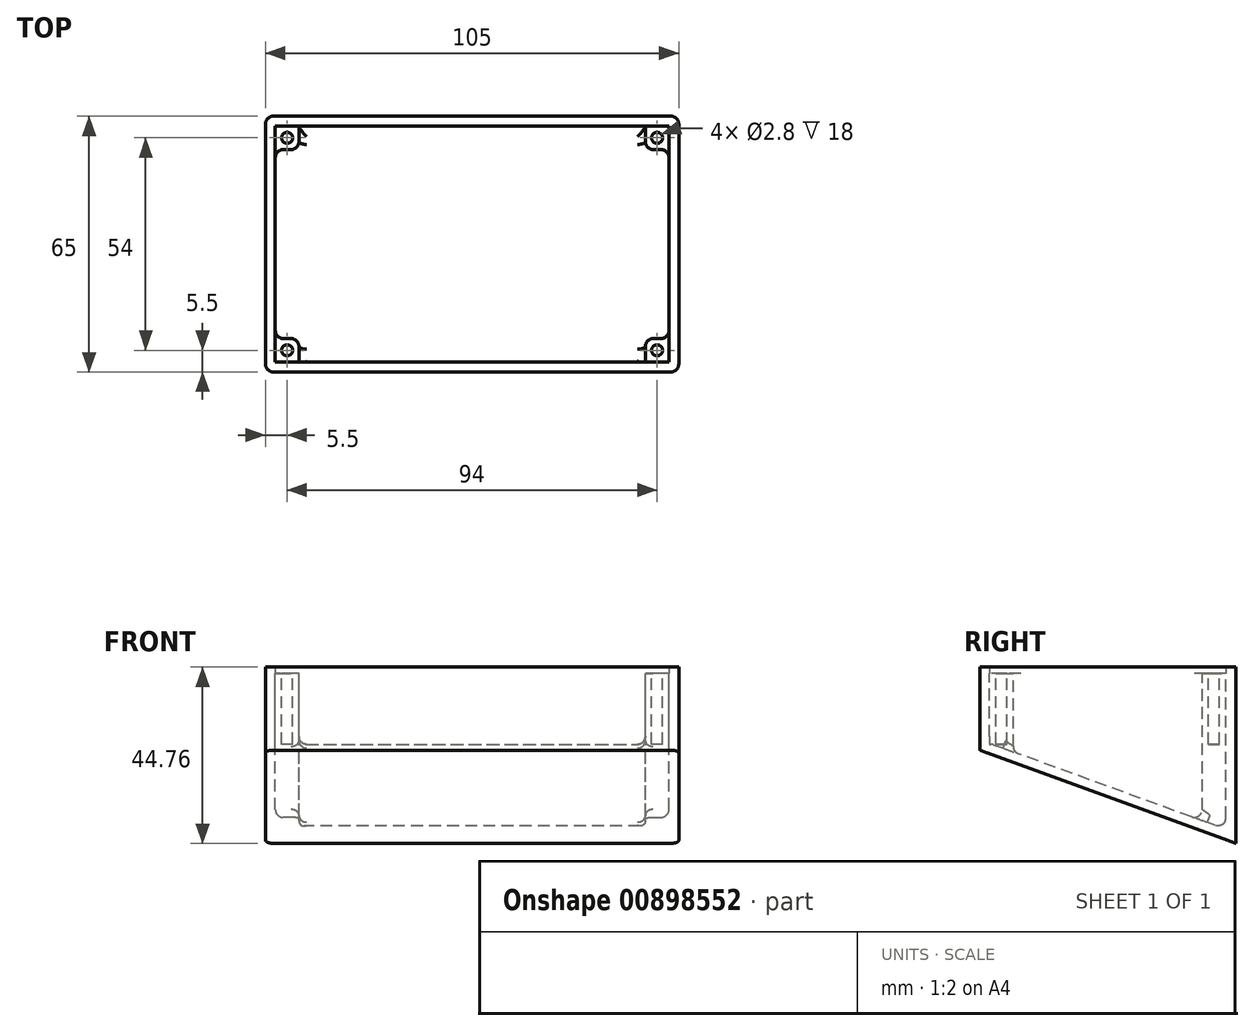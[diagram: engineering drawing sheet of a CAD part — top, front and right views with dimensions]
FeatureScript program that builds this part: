
annotation { "Feature Type Name" : "Feature", "Feature Type Description" : "" }
export const myFeature = defineFeature(function(context is Context, id is Id, definition is map)
    precondition{}
    {
        {
            var Q0;
            Q0=qCreatedBy(makeId("Top.planeOp"),FACE);
            var sketch = newSketch(context, id + "F0", { "sketchPlane" : qUnion([Q0])});
            skLineSegment(sketch, "E0", {"start": v(0, 30) * mm, "end": v(-50, 30) * mm});
            skLineSegment(sketch, "E1", {"start": v(-50, 30) * mm, "end": v(-50, 0) * mm});
            skLineSegment(sketch, "E2.MirrorCS", {"start": v(0, 30) * mm, "end": v(50, 30) * mm});
            skLineSegment(sketch, "E3.MirrorCS", {"start": v(50, 30) * mm, "end": v(50, 0) * mm});
            skLineSegment(sketch, "E4.MirrorCS", {"start": v(-50, -30) * mm, "end": v(-50, 0) * mm});
            skLineSegment(sketch, "E5.MirrorCS", {"start": v(0, -30) * mm, "end": v(-50, -30) * mm});
            skLineSegment(sketch, "E6.MirrorCS", {"start": v(0, -30) * mm, "end": v(50, -30) * mm});
            skLineSegment(sketch, "E7.MirrorCS", {"start": v(50, -30) * mm, "end": v(50, 0) * mm});
            skLineSegment(sketch, "E8", {"start": v(0, 32.5) * mm, "end": v(-52.5, 32.5) * mm});
            skLineSegment(sketch, "E9", {"start": v(-52.5, 32.5) * mm, "end": v(-52.5, 0) * mm});
            skLineSegment(sketch, "E10.MirrorCS", {"start": v(52.5, 32.5) * mm, "end": v(52.5, 0) * mm});
            skLineSegment(sketch, "E11.MirrorCS", {"start": v(0, 32.5) * mm, "end": v(52.5, 32.5) * mm});
            skLineSegment(sketch, "E12.MirrorCS", {"start": v(-52.5, -32.5) * mm, "end": v(-52.5, 0) * mm});
            skLineSegment(sketch, "E13.MirrorCS", {"start": v(0, -32.5) * mm, "end": v(-52.5, -32.5) * mm});
            skLineSegment(sketch, "E14.MirrorCS", {"start": v(0, -32.5) * mm, "end": v(52.5, -32.5) * mm});
            skLineSegment(sketch, "E15.MirrorCS", {"start": v(52.5, -32.5) * mm, "end": v(52.5, 0) * mm});
            skSolve(sketch);
        }
        {
            var Q0;
            Q0=makeQuery(id+"F0.imprint","IMPRINT",FACE,{"disambiguationData":[TD([[makeQuery(id+"F0.imprint","IMPRINT",EDGE,{"derivedFrom":sQuery(id+"F0.wireOp",EDGE,"E0")}),-1.0]])]});
            extrude(context, id + "F1", {"entities" : qUnion([Q0]), "depth" : 1.6 * mm, "offsetDistance" : 25 * mm});
        }
        {
            var Q0;
            Q0=qCreatedBy(makeId("Top.planeOp"),FACE);
            var sketch = newSketch(context, id + "F2", { "sketchPlane" : qUnion([Q0])});
            skLineSegment(sketch, "E16.0", {"start": v(-52.5, 32.5) * mm, "end": v(52.5, 32.5) * mm});
            skLineSegment(sketch, "E17.0", {"start": v(-52.5, 32.5) * mm, "end": v(-52.5, -32.5) * mm});
            skCircle(sketch, "E18", {"center": v(-47, 27) * mm, "radius": 1.4 * mm});
            skLineSegment(sketch, "E19", {"start": v(-50, 24) * mm, "end": v(-44, 24) * mm});
            skLineSegment(sketch, "E20", {"start": v(-44, 24) * mm, "end": v(-44, 30) * mm});
            skLineSegment(sketch, "E21.0", {"start": v(44, 30) * mm, "end": v(-44, 30) * mm});
            skLineSegment(sketch, "E22.0", {"start": v(-50, -30) * mm, "end": v(-50, 24) * mm});
            skPoint(sketch, "E23.orphan", {"position": v(-50, 30) * mm});
            skLineSegment(sketch, "E24.MirrorCS", {"start": v(-44, 30) * mm, "end": v(44, 30) * mm});
            skLineSegment(sketch, "E25.MirrorCS", {"start": v(52.5, 32.5) * mm, "end": v(-52.5, 32.5) * mm});
            skLineSegment(sketch, "E26.MirrorCS", {"start": v(44, 24) * mm, "end": v(44, 30) * mm});
            skLineSegment(sketch, "E27.MirrorCS", {"start": v(50, 24) * mm, "end": v(44, 24) * mm});
            skLineSegment(sketch, "E28.MirrorCS", {"start": v(52.5, 32.5) * mm, "end": v(52.5, -32.5) * mm});
            skLineSegment(sketch, "E29.MirrorCS", {"start": v(50, -30) * mm, "end": v(50, 24) * mm});
            skCircle(sketch, "E30.MirrorC", {"center": v(47, 27) * mm, "radius": 1.4 * mm});
            skPoint(sketch, "E31.orphan", {"position": v(50, 30) * mm});
            skLineSegment(sketch, "E32.MirrorCS", {"start": v(-50, 30) * mm, "end": v(-50, -24) * mm});
            skLineSegment(sketch, "E33.MirrorCS", {"start": v(-50, -24) * mm, "end": v(-44, -24) * mm});
            skLineSegment(sketch, "E34.MirrorCS", {"start": v(-44, -24) * mm, "end": v(-44, -30) * mm});
            skLineSegment(sketch, "E35.MirrorCS", {"start": v(-44, -30) * mm, "end": v(44, -30) * mm});
            skCircle(sketch, "E36.MirrorC", {"center": v(-47, -27) * mm, "radius": 1.4 * mm});
            skLineSegment(sketch, "E37.MirrorCS", {"start": v(52.5, -32.5) * mm, "end": v(-52.5, -32.5) * mm});
            skLineSegment(sketch, "E38.MirrorCS", {"start": v(-52.5, -32.5) * mm, "end": v(-52.5, 32.5) * mm});
            skLineSegment(sketch, "E39.MirrorCS", {"start": v(52.5, -32.5) * mm, "end": v(52.5, 32.5) * mm});
            skLineSegment(sketch, "E40.MirrorCS", {"start": v(50, -24) * mm, "end": v(44, -24) * mm});
            skLineSegment(sketch, "E41.MirrorCS", {"start": v(44, -24) * mm, "end": v(44, -30) * mm});
            skCircle(sketch, "E42.MirrorC", {"center": v(47, -27) * mm, "radius": 1.4 * mm});
            skSolve(sketch);
        }
        {
            var Q0;
            Q0 = qSketchRegion(id + "F2", true);
            extrude(context, id + "F3", {"entities" : qUnion([Q0]), "operationType" : NewBodyOperationType.ADD, "oppositeDirection" : true, "depth" : 18 * mm, "offsetDistance" : 25 * mm});
        }
        {
            var Q0;
            {var subQ0=sQuery(id+"F0.wireOp",EDGE,"E15.MirrorCS");var subQ1=sQuery(id+"F0.wireOp",EDGE,"E10.MirrorCS");Q0=makeQuery(id+"F3.boolean.opBoolean","MERGE",FACE,{"derivedFrom":[makeQuery(id+"F1.opExtrude","SWEPT_FACE",FACE,{"disambiguationData":[OSD([subQ1,subQ0])]}),makeQuery(id+"F3.opExtrude","SWEPT_FACE",FACE,{"disambiguationData":[OSD([subQ1,subQ0])]}),makeQuery(id+"F3.opExtrude","SWEPT_FACE",FACE,{"disambiguationData":[OSD([sQuery(id+"F2.wireOp",EDGE,"E39.MirrorCS")])]})]});}
            var sketch = newSketch(context, id + "F4", { "sketchPlane" : qUnion([Q0])});
            skLineSegment(sketch, "E43", {"start": v(-32.5, -18) * mm, "end": v(-32.5, -19.5) * mm});
            skLineSegment(sketch, "E44", {"start": v(-32.5, -19.5) * mm, "end": v(32.5, -43.16) * mm});
            skLineSegment(sketch, "E45", {"start": v(32.5, -43.16) * mm, "end": v(32.5, -18) * mm});
            skSolve(sketch);
        }
        {
            var Q0;
            Q0=makeQuery(id+"F4.imprint","IMPRINT",FACE,{"disambiguationData":[TD([[makeQuery(id+"F4.imprint","IMPRINT",EDGE,{"derivedFrom":sQuery(id+"F4.wireOp",EDGE,"E43")}),1.0]])]});
            extrude(context, id + "F5", {"entities" : qUnion([Q0]), "operationType" : NewBodyOperationType.ADD, "oppositeDirection" : true, "depth" : 1.5 * mm, "offsetDistance" : 25 * mm});
        }
        {
            var Q0;
            Q0=makeQuery(id+"F3.boolean.opBoolean","MERGE",FACE,{"derivedFrom":[makeQuery(id+"F1.opExtrude","SWEPT_FACE",FACE,{"disambiguationData":[OSD([sQuery(id+"F0.wireOp",EDGE,"E9"),sQuery(id+"F0.wireOp",EDGE,"E12.MirrorCS")])]}),makeQuery(id+"F3.opExtrude","SWEPT_FACE",FACE,{"disambiguationData":[OSD([sQuery(id+"F2.wireOp",EDGE,"E38.MirrorCS")])]})]});
            var sketch = newSketch(context, id + "F6", { "sketchPlane" : qUnion([Q0])});
            skLineSegment(sketch, "E46.0.3", {"start": v(-32.5, -43.16) * mm, "end": v(32.5, -19.5) * mm});
            skLineSegment(sketch, "E46.0.4", {"start": v(32.5, -19.5) * mm, "end": v(32.5, -18) * mm});
            skLineSegment(sketch, "E47.0", {"start": v(-32.5, -43.16) * mm, "end": v(-32.5, -18) * mm});
            skLineSegment(sketch, "E48", {"start": v(32.5, -18) * mm, "end": v(-32.5, -18) * mm});
            skLineSegment(sketch, "E49.0", {"start": v(32.5, -19.5) * mm, "end": v(-32.5, -43.16) * mm, "construction": true});
            skLineSegment(sketch, "E49.1", {"start": v(-32.5, 1.6) * mm, "end": v(-32.5, -43.16) * mm, "construction": true});
            skLineSegment(sketch, "E49.2", {"start": v(32.5, 1.6) * mm, "end": v(32.5, -19.5) * mm, "construction": true});
            skSolve(sketch);
        }
        {
            var Q0;
            Q0 = qSketchRegion(id + "F6", true);
            extrude(context, id + "F7", {"entities" : qUnion([Q0]), "operationType" : NewBodyOperationType.ADD, "oppositeDirection" : true, "depth" : 1.5 * mm, "offsetDistance" : 25 * mm});
        }
        {
            var Q0;
            Q0=makeQuery(id+"F5.opExtrude","CAP_FACE",FACE,{"disambiguationData":[OSD([sQuery(id+"F2.wireOp",EDGE,"E39.MirrorCS"),sQuery(id+"F4.wireOp",EDGE,"E43"),sQuery(id+"F4.wireOp",EDGE,"E44"),sQuery(id+"F4.wireOp",EDGE,"E45")])],"isStart":false});
            var sketch = newSketch(context, id + "F8", { "sketchPlane" : qUnion([Q0])});
            skLineSegment(sketch, "E50.0", {"start": v(-32.5, -43.16) * mm, "end": v(-32.5, -18) * mm});
            skLineSegment(sketch, "E51.0", {"start": v(32.5, -19.5) * mm, "end": v(-32.5, -43.16) * mm});
            skLineSegment(sketch, "E52.0", {"start": v(32.5, -18) * mm, "end": v(32.5, -19.5) * mm});
            skLineSegment(sketch, "E53", {"start": v(-30, -39.59) * mm, "end": v(29.31, -18) * mm});
            skLineSegment(sketch, "E54", {"start": v(-30, -18) * mm, "end": v(-30, -39.59) * mm});
            skLineSegment(sketch, "E55.0", {"start": v(-30, -18) * mm, "end": v(-32.5, -18) * mm});
            skLineSegment(sketch, "E56.0", {"start": v(32.5, -18) * mm, "end": v(-32.5, -18) * mm, "construction": true});
            skSolve(sketch);
        }
        {
            var Q0;
            Q0=makeQuery(id+"F8.imprint","IMPRINT",FACE,{"disambiguationData":[TD([[makeQuery(id+"F8.imprint","IMPRINT",EDGE,{"derivedFrom":sQuery(id+"F8.wireOp",EDGE,"E50.0")}),-1.0]])]});
            extrude(context, id + "F9", {"entities" : qUnion([Q0]), "operationType" : NewBodyOperationType.ADD, "endBound" : BoundingType.UP_TO_NEXT, "depth" : 25 * mm, "offsetDistance" : 25 * mm});
        }
        {
            var Q0;
            {var subQ0=sQuery(id+"F2.wireOp",EDGE,"E26.MirrorCS");var subQ1=makeQuery(id+"F3.opExtrude","SWEPT_FACE",FACE,{"disambiguationData":[OSD([subQ0])]});var subQ3=sQuery(id+"F2.wireOp",EDGE,"E39.MirrorCS");var subQ5=sQuery(id+"F2.wireOp",EDGE,"E24.MirrorCS");var subQ9=sQuery(id+"F2.wireOp",EDGE,"E27.MirrorCS");var subQ11=sQuery(id+"F2.wireOp",EDGE,"E29.MirrorCS");var subQ13=sQuery(id+"F2.wireOp",EDGE,"E30.MirrorC");var subQ15=sQuery(id+"F2.wireOp",EDGE,"E25.MirrorCS");var subQ16=sQuery(id+"F2.wireOp",EDGE,"E20");var subQ17=sQuery(id+"F2.wireOp",EDGE,"E18");var subQ18=sQuery(id+"F2.wireOp",EDGE,"E19");var subQ20=sQuery(id+"F2.wireOp",EDGE,"E32.MirrorCS");Q0=makeQuery(id+"F9.boolean.opBoolean","SPLIT",FACE,{"disambiguationData":[TD([subQ1])],"derivedFrom":makeQuery(id+"F7.boolean.opBoolean","SPLIT",FACE,{"disambiguationData":[TD([makeQuery(id+"F3.opExtrude","SWEPT_FACE",FACE,{"disambiguationData":[OSD([subQ17])]})])],"derivedFrom":makeQuery(id+"F3.opExtrude","CAP_FACE",FACE,{"disambiguationData":[OSD([subQ17,subQ18,subQ16,subQ5,subQ15,subQ0,subQ9,subQ11,subQ13,subQ20,sQuery(id+"F2.wireOp",EDGE,"E33.MirrorCS"),sQuery(id+"F2.wireOp",EDGE,"E34.MirrorCS"),sQuery(id+"F2.wireOp",EDGE,"E35.MirrorCS"),sQuery(id+"F2.wireOp",EDGE,"E36.MirrorC"),sQuery(id+"F2.wireOp",EDGE,"E37.MirrorCS"),sQuery(id+"F2.wireOp",EDGE,"E38.MirrorCS"),subQ3,sQuery(id+"F2.wireOp",EDGE,"E40.MirrorCS"),sQuery(id+"F2.wireOp",EDGE,"E41.MirrorCS"),sQuery(id+"F2.wireOp",EDGE,"E42.MirrorC")])],"isStart":false})})});}
            var sketch = newSketch(context, id + "F10", { "sketchPlane" : qUnion([Q0])});
            skLineSegment(sketch, "E57.0.0", {"start": v(-44, 30) * mm, "end": v(-50, 30) * mm});
            skLineSegment(sketch, "E57.0.1", {"start": v(-50, 30) * mm, "end": v(-50, 24) * mm});
            skLineSegment(sketch, "E57.0.2", {"start": v(-50, 24) * mm, "end": v(-44, 24) * mm});
            skLineSegment(sketch, "E57.0.3", {"start": v(-44, 24) * mm, "end": v(-44, 30) * mm});
            skLineSegment(sketch, "E58.0.0", {"start": v(-50, -24) * mm, "end": v(-50, -30) * mm});
            skLineSegment(sketch, "E58.0.1", {"start": v(-50, -30) * mm, "end": v(-44, -30) * mm});
            skLineSegment(sketch, "E58.0.2", {"start": v(-44, -30) * mm, "end": v(-44, -24) * mm});
            skLineSegment(sketch, "E58.0.3", {"start": v(-44, -24) * mm, "end": v(-50, -24) * mm});
            skLineSegment(sketch, "E59.0.2", {"start": v(44, 24) * mm, "end": v(50, 24) * mm});
            skLineSegment(sketch, "E60.0", {"start": v(-50, 30) * mm, "end": v(-50, -30) * mm, "construction": true});
            skLineSegment(sketch, "E61", {"start": v(50, 24) * mm, "end": v(50, 30) * mm});
            skLineSegment(sketch, "E62", {"start": v(50, 30) * mm, "end": v(44, 30) * mm});
            skLineSegment(sketch, "E63", {"start": v(44, 30) * mm, "end": v(44, 24) * mm});
            skLineSegment(sketch, "E64.bottom", {"start": v(44, -24) * mm, "end": v(50, -24) * mm});
            skLineSegment(sketch, "E64.top", {"start": v(44, -30) * mm, "end": v(50, -30) * mm});
            skLineSegment(sketch, "E64.left", {"start": v(44, -24) * mm, "end": v(44, -30) * mm});
            skLineSegment(sketch, "E64.right", {"start": v(50, -24) * mm, "end": v(50, -30) * mm});
            skLineSegment(sketch, "E65", {"start": v(-50, 24) * mm, "end": v(-50, -24) * mm});
            skLineSegment(sketch, "E66", {"start": v(-51, -30) * mm, "end": v(-51, 30) * mm});
            skLineSegment(sketch, "E67", {"start": v(-51, 30) * mm, "end": v(-50, 30) * mm});
            skLineSegment(sketch, "E68", {"start": v(-50, -30) * mm, "end": v(-51, -30) * mm});
            skLineSegment(sketch, "E69.0", {"start": v(-51, -30) * mm, "end": v(-51, 29.31) * mm, "construction": true});
            skLineSegment(sketch, "E70.0", {"start": v(51, -30) * mm, "end": v(51, 29.31) * mm, "construction": true});
            skLineSegment(sketch, "E71.bottom", {"start": v(50, 30) * mm, "end": v(51, 30) * mm});
            skLineSegment(sketch, "E71.top", {"start": v(50, -30) * mm, "end": v(51, -30) * mm});
            skLineSegment(sketch, "E71.left", {"start": v(50, 30) * mm, "end": v(50, -30) * mm});
            skLineSegment(sketch, "E71.right", {"start": v(51, 30) * mm, "end": v(51, -30) * mm});
            skSolve(sketch);
        }
        {
            var Q0;
            Q0 = qSketchRegion(id + "F10", true);
            extrude(context, id + "F11", {"entities" : qUnion([Q0]), "operationType" : NewBodyOperationType.ADD, "endBound" : BoundingType.UP_TO_NEXT, "depth" : 25 * mm, "offsetDistance" : 25 * mm});
        }
        {
            var Q0;
            {var subQ0=sQuery(id+"F2.wireOp",EDGE,"E35.MirrorCS");var subQ1=sQuery(id+"F2.wireOp",EDGE,"E34.MirrorCS");Q0=makeQuery(id+"F11.boolean.opBoolean","MERGE",EDGE,{"derivedFrom":[makeQuery(id+"F3.opExtrude","SWEPT_EDGE",EDGE,{"disambiguationData":[OSD([subQ1,subQ0])]}),makeQuery(id+"F11.opExtrude","SWEPT_EDGE",EDGE,{"disambiguationData":[OSD([subQ1,subQ0,sQuery(id+"F10.wireOp",EDGE,"E57.0.0"),sQuery(id+"F10.wireOp",EDGE,"E57.0.3")])]})]});}
            var Q1;
            {var subQ0=sQuery(id+"F2.wireOp",EDGE,"E34.MirrorCS");var subQ1=sQuery(id+"F2.wireOp",EDGE,"E33.MirrorCS");Q1=makeQuery(id+"F11.boolean.opBoolean","MERGE",EDGE,{"derivedFrom":[makeQuery(id+"F3.opExtrude","SWEPT_EDGE",EDGE,{"disambiguationData":[OSD([subQ1,subQ0])]}),makeQuery(id+"F11.opExtrude","SWEPT_EDGE",EDGE,{"disambiguationData":[OSD([subQ1,subQ0,sQuery(id+"F10.wireOp",EDGE,"E57.0.2"),sQuery(id+"F10.wireOp",EDGE,"E57.0.3")])]})]});}
            var Q2;
            {var subQ0=sQuery(id+"F2.wireOp",EDGE,"E33.MirrorCS");var subQ1=sQuery(id+"F2.wireOp",EDGE,"E32.MirrorCS");Q2=makeQuery(id+"F11.boolean.opBoolean","MERGE",EDGE,{"derivedFrom":[makeQuery(id+"F3.opExtrude","SWEPT_EDGE",EDGE,{"disambiguationData":[OSD([subQ1,subQ0])]}),makeQuery(id+"F11.opExtrude","SWEPT_EDGE",EDGE,{"disambiguationData":[OSD([subQ1,subQ0,sQuery(id+"F10.wireOp",EDGE,"E57.0.1"),sQuery(id+"F10.wireOp",EDGE,"E57.0.2")])]})]});}
            var Q3;
            {var subQ0=sQuery(id+"F2.wireOp",EDGE,"E20");var subQ1=sQuery(id+"F2.wireOp",EDGE,"E19");Q3=makeQuery(id+"F11.boolean.opBoolean","MERGE",EDGE,{"derivedFrom":[makeQuery(id+"F3.opExtrude","SWEPT_EDGE",EDGE,{"disambiguationData":[OSD([subQ1,subQ0])]}),makeQuery(id+"F11.opExtrude","SWEPT_EDGE",EDGE,{"disambiguationData":[OSD([subQ1,subQ0,sQuery(id+"F10.wireOp",EDGE,"E58.0.2"),sQuery(id+"F10.wireOp",EDGE,"E58.0.3")])]})]});}
            var Q4;
            {var subQ0=sQuery(id+"F2.wireOp",EDGE,"E32.MirrorCS");var subQ1=sQuery(id+"F2.wireOp",EDGE,"E19");Q4=makeQuery(id+"F11.boolean.opBoolean","MERGE",EDGE,{"derivedFrom":[makeQuery(id+"F3.opExtrude","SWEPT_EDGE",EDGE,{"disambiguationData":[OSD([subQ1,subQ0])]}),makeQuery(id+"F11.opExtrude","SWEPT_EDGE",EDGE,{"disambiguationData":[OSD([subQ1,subQ0,sQuery(id+"F10.wireOp",EDGE,"E58.0.0"),sQuery(id+"F10.wireOp",EDGE,"E58.0.3")])]})]});}
            var Q5;
            {var subQ0=sQuery(id+"F2.wireOp",EDGE,"E24.MirrorCS");var subQ1=sQuery(id+"F2.wireOp",EDGE,"E20");Q5=makeQuery(id+"F11.boolean.opBoolean","MERGE",EDGE,{"derivedFrom":[makeQuery(id+"F3.opExtrude","SWEPT_EDGE",EDGE,{"disambiguationData":[OSD([subQ1,subQ0])]}),makeQuery(id+"F11.opExtrude","SWEPT_EDGE",EDGE,{"disambiguationData":[OSD([subQ1,subQ0,sQuery(id+"F10.wireOp",EDGE,"E58.0.1"),sQuery(id+"F10.wireOp",EDGE,"E58.0.2")])]})]});}
            var Q6;
            {var subQ0=sQuery(id+"F2.wireOp",EDGE,"E27.MirrorCS");var subQ1=sQuery(id+"F2.wireOp",EDGE,"E26.MirrorCS");Q6=makeQuery(id+"F11.boolean.opBoolean","MERGE",EDGE,{"derivedFrom":[makeQuery(id+"F3.opExtrude","SWEPT_EDGE",EDGE,{"disambiguationData":[OSD([subQ1,subQ0])]}),makeQuery(id+"F11.opExtrude","SWEPT_EDGE",EDGE,{"disambiguationData":[OSD([subQ1,subQ0,sQuery(id+"F10.wireOp",EDGE,"f420157c-72c5-42ba-b6a2-5769d05b04c3.0.0"),sQuery(id+"F10.wireOp",EDGE,"f420157c-72c5-42ba-b6a2-5769d05b04c3.0.3")])]})]});}
            var Q7;
            {var subQ0=sQuery(id+"F2.wireOp",EDGE,"E26.MirrorCS");var subQ1=sQuery(id+"F2.wireOp",EDGE,"E24.MirrorCS");Q7=makeQuery(id+"F11.boolean.opBoolean","MERGE",EDGE,{"derivedFrom":[makeQuery(id+"F3.opExtrude","SWEPT_EDGE",EDGE,{"disambiguationData":[OSD([subQ1,subQ0])]}),makeQuery(id+"F11.opExtrude","SWEPT_EDGE",EDGE,{"disambiguationData":[OSD([subQ1,subQ0,sQuery(id+"F10.wireOp",EDGE,"f420157c-72c5-42ba-b6a2-5769d05b04c3.0.0"),sQuery(id+"F10.wireOp",EDGE,"f420157c-72c5-42ba-b6a2-5769d05b04c3.0.1")])]})]});}
            var Q8;
            {var subQ0=sQuery(id+"F2.wireOp",EDGE,"E29.MirrorCS");var subQ1=sQuery(id+"F2.wireOp",EDGE,"E27.MirrorCS");Q8=makeQuery(id+"F11.boolean.opBoolean","MERGE",EDGE,{"derivedFrom":[makeQuery(id+"F3.opExtrude","SWEPT_EDGE",EDGE,{"disambiguationData":[OSD([subQ1,subQ0])]}),makeQuery(id+"F11.opExtrude","SWEPT_EDGE",EDGE,{"disambiguationData":[OSD([subQ1,subQ0,sQuery(id+"F10.wireOp",EDGE,"f420157c-72c5-42ba-b6a2-5769d05b04c3.0.2"),sQuery(id+"F10.wireOp",EDGE,"f420157c-72c5-42ba-b6a2-5769d05b04c3.0.3")])]})]});}
            var Q9;
            {var subQ0=sQuery(id+"F2.wireOp",EDGE,"E40.MirrorCS");var subQ1=sQuery(id+"F2.wireOp",EDGE,"E29.MirrorCS");Q9=makeQuery(id+"F11.boolean.opBoolean","MERGE",EDGE,{"derivedFrom":[makeQuery(id+"F3.opExtrude","SWEPT_EDGE",EDGE,{"disambiguationData":[OSD([subQ1,subQ0])]}),makeQuery(id+"F11.opExtrude","SWEPT_EDGE",EDGE,{"disambiguationData":[OSD([subQ1,subQ0,sQuery(id+"F10.wireOp",EDGE,"E59.0.2"),sQuery(id+"F10.wireOp",EDGE,"E59.0.3")])]})]});}
            var Q10;
            {var subQ0=sQuery(id+"F2.wireOp",EDGE,"E41.MirrorCS");var subQ1=sQuery(id+"F2.wireOp",EDGE,"E40.MirrorCS");Q10=makeQuery(id+"F11.boolean.opBoolean","MERGE",EDGE,{"derivedFrom":[makeQuery(id+"F3.opExtrude","SWEPT_EDGE",EDGE,{"disambiguationData":[OSD([subQ1,subQ0])]}),makeQuery(id+"F11.opExtrude","SWEPT_EDGE",EDGE,{"disambiguationData":[OSD([subQ1,subQ0,sQuery(id+"F10.wireOp",EDGE,"E59.0.1"),sQuery(id+"F10.wireOp",EDGE,"E59.0.2")])]})]});}
            var Q11;
            {var subQ0=sQuery(id+"F2.wireOp",EDGE,"E41.MirrorCS");var subQ1=sQuery(id+"F2.wireOp",EDGE,"E35.MirrorCS");Q11=makeQuery(id+"F11.boolean.opBoolean","MERGE",EDGE,{"derivedFrom":[makeQuery(id+"F3.opExtrude","SWEPT_EDGE",EDGE,{"disambiguationData":[OSD([subQ1,subQ0])]}),makeQuery(id+"F11.opExtrude","SWEPT_EDGE",EDGE,{"disambiguationData":[OSD([subQ1,subQ0,sQuery(id+"F10.wireOp",EDGE,"E59.0.0"),sQuery(id+"F10.wireOp",EDGE,"E59.0.1")])]})]});}
            var Q12;
            Q12=makeQuery(id+"F9.opExtrude","SWEPT_FACE",FACE,{"disambiguationData":[OSD([sQuery(id+"F8.wireOp",EDGE,"E53")])]});
            fillet(context, id + "F12", {"entities" : qUnion([Q0, Q1, Q2, Q3, Q4, Q5, Q6, Q7, Q8, Q9, Q10, Q11, Q12]), "radius" : 2 * mm, "tangentPropagation" : true, "allowEdgeOverflow" : false});
        }
        {
            var Q0;
            Q0=makeQuery(id+"F7.boolean.opBoolean","MERGE",EDGE,{"derivedFrom":[makeQuery(id+"F3.boolean.opBoolean","MERGE",EDGE,{"derivedFrom":[makeQuery(id+"F1.opExtrude","SWEPT_EDGE",EDGE,{"disambiguationData":[OSD([sQuery(id+"F0.wireOp",EDGE,"E12.MirrorCS"),sQuery(id+"F0.wireOp",EDGE,"E13.MirrorCS")])]}),makeQuery(id+"F3.opExtrude","SWEPT_EDGE",EDGE,{"disambiguationData":[OSD([sQuery(id+"F2.wireOp",EDGE,"E37.MirrorCS"),sQuery(id+"F2.wireOp",EDGE,"E38.MirrorCS")])]})]}),makeQuery(id+"F7.opExtrude","CAP_EDGE",EDGE,{"disambiguationData":[OSD([sQuery(id+"F6.wireOp",EDGE,"E46.0.4")])],"isStart":true})]});
            var Q1;
            Q1=makeQuery(id+"F7.boolean.opBoolean","MERGE",EDGE,{"derivedFrom":[makeQuery(id+"F3.boolean.opBoolean","MERGE",EDGE,{"derivedFrom":[makeQuery(id+"F1.opExtrude","SWEPT_EDGE",EDGE,{"disambiguationData":[OSD([sQuery(id+"F0.wireOp",EDGE,"E8"),sQuery(id+"F0.wireOp",EDGE,"E9")])]}),makeQuery(id+"F3.opExtrude","SWEPT_EDGE",EDGE,{"disambiguationData":[OSD([sQuery(id+"F2.wireOp",EDGE,"E25.MirrorCS"),sQuery(id+"F2.wireOp",EDGE,"E38.MirrorCS")])]})]}),makeQuery(id+"F7.opExtrude","CAP_EDGE",EDGE,{"disambiguationData":[OSD([sQuery(id+"F6.wireOp",EDGE,"E47.0")])],"isStart":true})]});
            var Q2;
            Q2=makeQuery(id+"F5.boolean.opBoolean","MERGE",EDGE,{"derivedFrom":[makeQuery(id+"F3.boolean.opBoolean","MERGE",EDGE,{"derivedFrom":[makeQuery(id+"F1.opExtrude","SWEPT_EDGE",EDGE,{"disambiguationData":[OSD([sQuery(id+"F0.wireOp",EDGE,"E10.MirrorCS"),sQuery(id+"F0.wireOp",EDGE,"E11.MirrorCS")])]}),makeQuery(id+"F3.opExtrude","SWEPT_EDGE",EDGE,{"disambiguationData":[OSD([sQuery(id+"F2.wireOp",EDGE,"E25.MirrorCS"),sQuery(id+"F2.wireOp",EDGE,"E39.MirrorCS")])]})]}),makeQuery(id+"F5.opExtrude","CAP_EDGE",EDGE,{"disambiguationData":[OSD([sQuery(id+"F4.wireOp",EDGE,"E45")])],"isStart":true})]});
            var Q3;
            Q3=makeQuery(id+"F5.boolean.opBoolean","MERGE",EDGE,{"derivedFrom":[makeQuery(id+"F3.boolean.opBoolean","MERGE",EDGE,{"derivedFrom":[makeQuery(id+"F1.opExtrude","SWEPT_EDGE",EDGE,{"disambiguationData":[OSD([sQuery(id+"F0.wireOp",EDGE,"E14.MirrorCS"),sQuery(id+"F0.wireOp",EDGE,"E15.MirrorCS")])]}),makeQuery(id+"F3.opExtrude","SWEPT_EDGE",EDGE,{"disambiguationData":[OSD([sQuery(id+"F2.wireOp",EDGE,"E37.MirrorCS"),sQuery(id+"F2.wireOp",EDGE,"E39.MirrorCS")])]})]}),makeQuery(id+"F5.opExtrude","CAP_EDGE",EDGE,{"disambiguationData":[OSD([sQuery(id+"F4.wireOp",EDGE,"E43")])],"isStart":true})]});
            fillet(context, id + "F13", {"entities" : qUnion([Q0, Q1, Q2, Q3]), "radius" : 2 * mm, "tangentPropagation" : true, "allowEdgeOverflow" : false});
        }
    });
